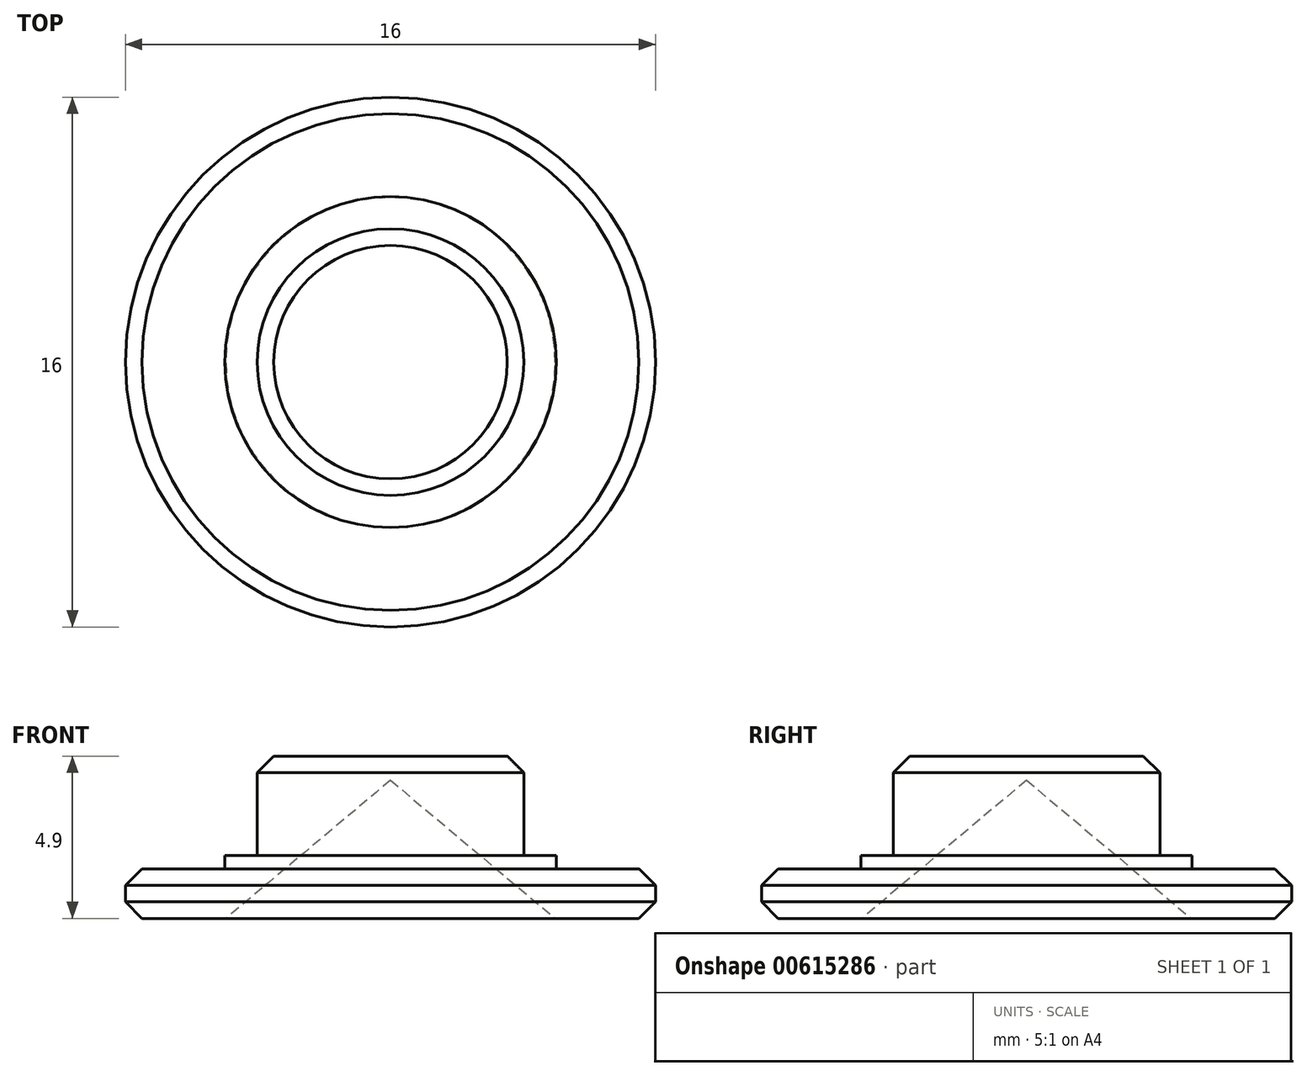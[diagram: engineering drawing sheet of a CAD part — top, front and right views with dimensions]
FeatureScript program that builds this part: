
annotation { "Feature Type Name" : "Feature", "Feature Type Description" : "" }
export const myFeature = defineFeature(function(context is Context, id is Id, definition is map)
    precondition{}
    {
        {
            var Q0;
            Q0=qCreatedBy(makeId("Top.planeOp"),FACE);
            var sketch = newSketch(context, id + "F0", { "sketchPlane" : qUnion([Q0])});
            skCircle(sketch, "E0", {"center": v(0, 0) * mm, "radius": 8 * mm});
            skSolve(sketch);
        }
        {
            var Q0;
            Q0 = qSketchRegion(id + "F0", true);
            extrude(context, id + "F1", {"entities" : qUnion([Q0]), "depth" : 1.5 * mm, "offsetDistance" : 25 * mm});
        }
        {
            var Q0;
            Q0=makeQuery(id+"F1.opExtrude","CAP_FACE",FACE,{"disambiguationData":[OSD([sQuery(id+"F0.wireOp",EDGE,"E0")])],"isStart":false});
            var sketch = newSketch(context, id + "F2", { "sketchPlane" : qUnion([Q0])});
            skCircle(sketch, "E1", {"center": v(0, 0) * mm, "radius": 5 * mm});
            skSolve(sketch);
        }
        {
            var Q0;
            Q0 = qSketchRegion(id + "F2", true);
            extrude(context, id + "F3", {"entities" : qUnion([Q0]), "operationType" : NewBodyOperationType.ADD, "depth" : 0.4 * mm, "offsetDistance" : 25 * mm});
        }
        {
            var Q0;
            Q0=makeQuery(id+"F3.opExtrude","CAP_FACE",FACE,{"disambiguationData":[OSD([sQuery(id+"F2.wireOp",EDGE,"E1")])],"isStart":false});
            var sketch = newSketch(context, id + "F4", { "sketchPlane" : qUnion([Q0])});
            skCircle(sketch, "E2", {"center": v(0, 0) * mm, "radius": 4.03 * mm});
            skSolve(sketch);
        }
        {
            var Q0;
            Q0 = qSketchRegion(id + "F4", true);
            extrude(context, id + "F5", {"entities" : qUnion([Q0]), "operationType" : NewBodyOperationType.ADD, "depth" : 3 * mm, "offsetDistance" : 25 * mm});
        }
        {
            var Q0;
            Q0=makeQuery(id+"F1.opExtrude","CAP_EDGE",EDGE,{"disambiguationData":[OSD([sQuery(id+"F0.wireOp",EDGE,"E0")])],"isStart":true});
            var Q1;
            Q1=makeQuery(id+"F1.opExtrude","CAP_EDGE",EDGE,{"disambiguationData":[OSD([sQuery(id+"F0.wireOp",EDGE,"E0")])],"isStart":false});
            var Q2;
            Q2=makeQuery(id+"F5.opExtrude","CAP_EDGE",EDGE,{"disambiguationData":[OSD([sQuery(id+"F4.wireOp",EDGE,"E2")])],"isStart":false});
            chamfer(context, id + "F6", {"entities" : qUnion([Q0, Q1, Q2]), "width" : 0.5 * mm, "tangentPropagation" : true});
        }
        {
            var Q0;
            Q0=qCreatedBy(makeId("Front.planeOp"),FACE);
            var sketch = newSketch(context, id + "F7", { "sketchPlane" : qUnion([Q0])});
            skLineSegment(sketch, "E3", {"start": v(-4.97, 0) * mm, "end": v(0, 4.17) * mm});
            skLineSegment(sketch, "E4", {"start": v(0, 4.17) * mm, "end": v(0, 0) * mm});
            skLineSegment(sketch, "E5", {"start": v(0, 0) * mm, "end": v(-4.97, 0) * mm});
            skSolve(sketch);
        }
        {
            var Q0;
            Q0 = qSketchRegion(id + "F7", true);
            var Q1;
            Q1=sQuery(id+"F7.wireOp",EDGE,"E4");
            revolve(context, id + "F8", {"operationType" : NewBodyOperationType.REMOVE, "entities" : qUnion([Q0]), "axis" : qUnion([Q1]), "revolveType" : RevolveType.FULL, "oppositeDirection" : true});
        }
    });
